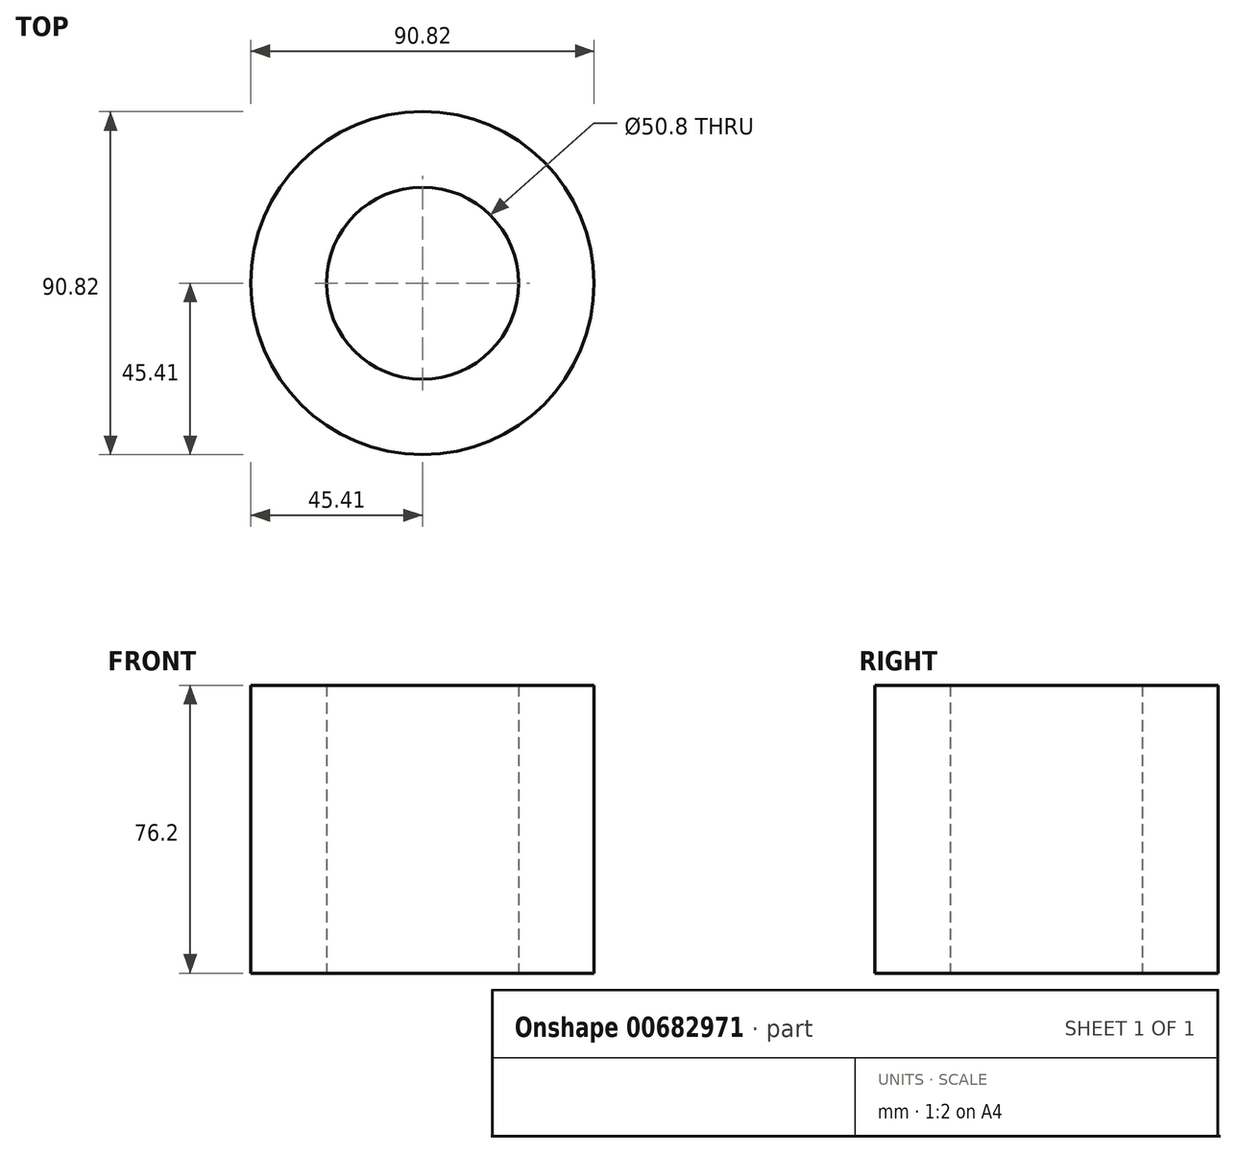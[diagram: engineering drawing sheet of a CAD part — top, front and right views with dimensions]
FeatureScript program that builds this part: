
annotation { "Feature Type Name" : "Feature", "Feature Type Description" : "" }
export const myFeature = defineFeature(function(context is Context, id is Id, definition is map)
    precondition{}
    {
        {
            var Q0;
            Q0=qCreatedBy(makeId("Top.planeOp"),FACE);
            var sketch = newSketch(context, id + "F0", { "sketchPlane" : qUnion([Q0])});
            skCircle(sketch, "E0", {"center": v(0, 0) * mm, "radius": 45.4 * mm});
            skCircle(sketch, "E1", {"center": v(0, 0) * mm, "radius": 25.4 * mm});
            skSolve(sketch);
        }
        {
            var Q0;
            Q0=makeQuery(id+"F0.imprint","IMPRINT",FACE,{"disambiguationData":[TD([[makeQuery(id+"F0.imprint","IMPRINT",EDGE,{"derivedFrom":sQuery(id+"F0.wireOp",EDGE,"E0")}),1.0]])]});
            extrude(context, id + "F1", {"entities" : qUnion([Q0]), "depth" : 76.2 * mm, "offsetDistance" : 25.4 * mm});
        }
    });
